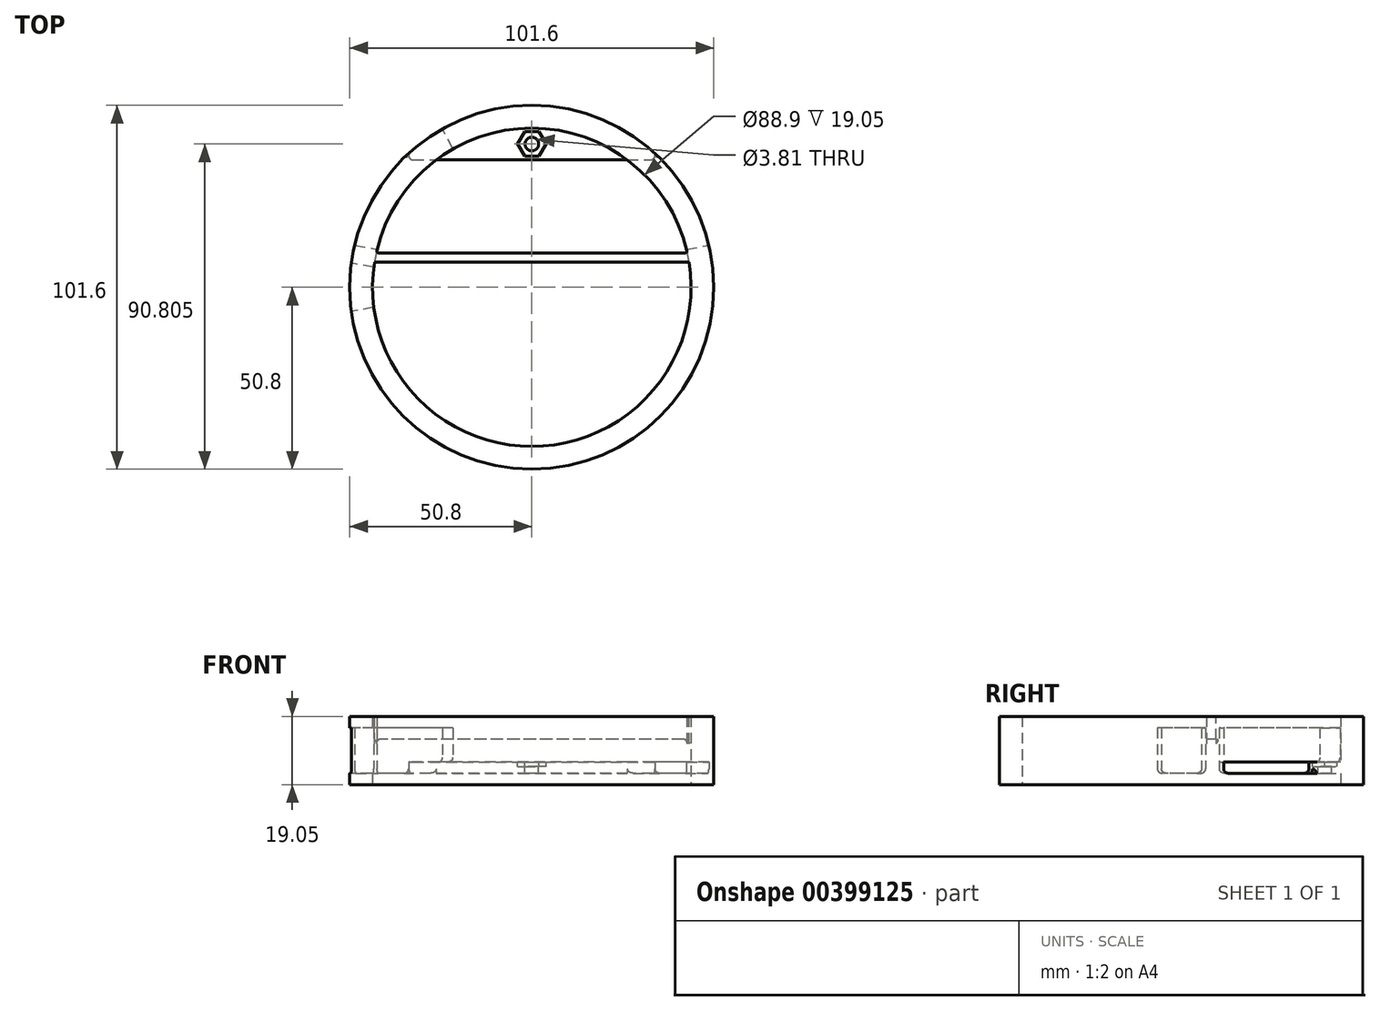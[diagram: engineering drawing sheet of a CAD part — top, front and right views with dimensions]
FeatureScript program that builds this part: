
annotation { "Feature Type Name" : "Feature", "Feature Type Description" : "" }
export const myFeature = defineFeature(function(context is Context, id is Id, definition is map)
    precondition{}
    {
        {
            var Q0;
            Q0=qCreatedBy(makeId("Top.planeOp"),FACE);
            var sketch = newSketch(context, id + "F0", { "sketchPlane" : qUnion([Q0])});
            skCircle(sketch, "E0", {"center": v(0, 0) * mm, "radius": 50.8 * mm});
            skCircle(sketch, "E1", {"center": v(0, 0) * mm, "radius": 44.45 * mm});
            skSolve(sketch);
        }
        {
            var Q0;
            Q0 = qSketchRegion(id + "F0", true);
            extrude(context, id + "F1", {"entities" : qUnion([Q0]), "depth" : 6.35 * mm});
        }
        {
            var Q0;
            Q0=makeQuery(id+"F1.opExtrude","CAP_FACE",FACE,{"disambiguationData":[OSD([sQuery(id+"F0.wireOp",EDGE,"E0"),sQuery(id+"F0.wireOp",EDGE,"E1")])],"isStart":false});
            var sketch = newSketch(context, id + "F2", { "sketchPlane" : qUnion([Q0])});
            skArc(sketch, "E2.0", {"start": v(26.67, 35.56) * mm, "mid": v(0, 44.45) * mm, "end": v(-26.67, 35.56) * mm});
            skLineSegment(sketch, "E3", {"start": v(-26.67, 35.56) * mm, "end": v(26.67, 35.56) * mm});
            skSolve(sketch);
        }
        {
            var Q0;
            Q0 = qSketchRegion(id + "F2", true);
            extrude(context, id + "F3", {"entities" : qUnion([Q0]), "operationType" : NewBodyOperationType.ADD, "oppositeDirection" : true, "depth" : 3.17 * mm});
        }
        {
            var Q0;
            {var subQ0=sQuery(id+"F2.wireOp",EDGE,"E3");var subQ1=sQuery(id+"F2.wireOp",EDGE,"E2.0");Q0=makeQuery(id+"FSnzgjkxEc41RKG_1.1.F3.boolean.opBoolean","MERGE",FACE,{"derivedFrom":[makeQuery(id+"F3.boolean.opBoolean","MERGE",FACE,{"derivedFrom":[makeQuery(id+"F1.opExtrude","CAP_FACE",FACE,{"disambiguationData":[OSD([sQuery(id+"F0.wireOp",EDGE,"E0"),sQuery(id+"F0.wireOp",EDGE,"E1")])],"isStart":false}),makeQuery(id+"F3.opExtrude","CAP_FACE",FACE,{"disambiguationData":[OSD([subQ1,subQ0])],"isStart":true})]}),makeQuery(id+"FSnzgjkxEc41RKG_1.1.F3.opExtrude","CAP_FACE",FACE,{"disambiguationData":[OSD([subQ1,subQ0])],"isStart":true})]});}
            var sketch = newSketch(context, id + "F4", { "sketchPlane" : qUnion([Q0])});
            skCircle(sketch, "E4.cCircle", {"center": v(0, 40) * mm, "radius": 3.43 * mm, "construction": true});
            skLineSegment(sketch, "E4.0", {"start": v(-1.98, 43.43) * mm, "end": v(1.98, 43.43) * mm});
            skLineSegment(sketch, "E4.1", {"start": v(1.98, 43.43) * mm, "end": v(3.96, 40) * mm});
            skLineSegment(sketch, "E4.2", {"start": v(3.96, 40) * mm, "end": v(1.98, 36.58) * mm});
            skLineSegment(sketch, "E4.3", {"start": v(1.98, 36.58) * mm, "end": v(-1.98, 36.58) * mm});
            skLineSegment(sketch, "E4.4", {"start": v(-1.98, 36.58) * mm, "end": v(-3.96, 40) * mm});
            skLineSegment(sketch, "E4.5", {"start": v(-3.96, 40) * mm, "end": v(-1.98, 43.43) * mm});
            skPoint(sketch, "E4.0.midPoint", {"position": v(0, 43.43) * mm});
            skSolve(sketch);
        }
        {
            var Q0;
            Q0 = qSketchRegion(id + "F4", true);
            extrude(context, id + "F5", {"entities" : qUnion([Q0]), "operationType" : NewBodyOperationType.REMOVE, "oppositeDirection" : true, "depth" : 1.27 * mm});
        }
        {
            var Q0;
            {var subQ0=sQuery(id+"F2.wireOp",EDGE,"E3");var subQ1=sQuery(id+"F2.wireOp",EDGE,"E2.0");Q0=makeQuery(id+"FSnzgjkxEc41RKG_1.1.F3.boolean.opBoolean","MERGE",FACE,{"derivedFrom":[makeQuery(id+"F3.boolean.opBoolean","MERGE",FACE,{"derivedFrom":[makeQuery(id+"F1.opExtrude","CAP_FACE",FACE,{"disambiguationData":[OSD([sQuery(id+"F0.wireOp",EDGE,"E0"),sQuery(id+"F0.wireOp",EDGE,"E1")])],"isStart":false}),makeQuery(id+"F3.opExtrude","CAP_FACE",FACE,{"disambiguationData":[OSD([subQ1,subQ0])],"isStart":true})]}),makeQuery(id+"FSnzgjkxEc41RKG_1.1.F3.opExtrude","CAP_FACE",FACE,{"disambiguationData":[OSD([subQ1,subQ0])],"isStart":true})]});}
            var sketch = newSketch(context, id + "F6", { "sketchPlane" : qUnion([Q0])});
            skCircle(sketch, "E5", {"center": v(0, 40) * mm, "radius": 3.43 * mm, "construction": true});
            skCircle(sketch, "E6", {"center": v(0, 40) * mm, "radius": 1.9 * mm});
            skSolve(sketch);
        }
        {
            var Q0;
            Q0 = qSketchRegion(id + "F6", true);
            extrude(context, id + "F7", {"entities" : qUnion([Q0]), "operationType" : NewBodyOperationType.REMOVE, "endBound" : BoundingType.THROUGH_ALL, "oppositeDirection" : true, "depth" : 25.4 * mm});
        }
        {
            var Q0;
            {var subQ0=sQuery(id+"F2.wireOp",EDGE,"E3");var subQ1=sQuery(id+"F2.wireOp",EDGE,"E2.0");Q0=makeQuery(id+"FSnzgjkxEc41RKG_1.1.F3.boolean.opBoolean","MERGE",FACE,{"derivedFrom":[makeQuery(id+"F3.boolean.opBoolean","MERGE",FACE,{"derivedFrom":[makeQuery(id+"F1.opExtrude","CAP_FACE",FACE,{"disambiguationData":[OSD([sQuery(id+"F0.wireOp",EDGE,"E0"),sQuery(id+"F0.wireOp",EDGE,"E1")])],"isStart":false}),makeQuery(id+"F3.opExtrude","CAP_FACE",FACE,{"disambiguationData":[OSD([subQ1,subQ0])],"isStart":true})]}),makeQuery(id+"FSnzgjkxEc41RKG_1.1.F3.opExtrude","CAP_FACE",FACE,{"disambiguationData":[OSD([subQ1,subQ0])],"isStart":true})]});}
            var sketch = newSketch(context, id + "F8", { "sketchPlane" : qUnion([Q0])});
            skCircle(sketch, "E7", {"center": v(0, 0) * mm, "radius": 44.45 * mm});
            skCircle(sketch, "E8.0", {"center": v(0, 0) * mm, "radius": 50.8 * mm});
            skSolve(sketch);
        }
        {
            var Q0;
            Q0 = qSketchRegion(id + "F8", true);
            extrude(context, id + "F9", {"entities" : qUnion([Q0]), "operationType" : NewBodyOperationType.ADD, "depth" : 9.52 * mm});
        }
        {
            var Q0;
            Q0=makeQuery(id+"F9.opExtrude","CAP_FACE",FACE,{"disambiguationData":[OSD([sQuery(id+"F8.wireOp",EDGE,"E7"),sQuery(id+"F8.wireOp",EDGE,"E8.0")])],"isStart":false});
            var sketch = newSketch(context, id + "F10", { "sketchPlane" : qUnion([Q0])});
            skLineSegment(sketch, "E9", {"start": v(0, 0) * mm, "end": v(-63.41, 11.75) * mm, "construction": true});
            skLineSegment(sketch, "E10", {"start": v(0, 0) * mm, "end": v(-59.62, -11.05) * mm, "construction": true});
            skLineSegment(sketch, "E11.0", {"start": v(-13.94, 0) * mm, "end": v(-56.67, 7.92) * mm});
            skLineSegment(sketch, "E11.1", {"start": v(-13.94, 0) * mm, "end": v(-56.67, -7.92) * mm});
            skLineSegment(sketch, "E12", {"start": v(-56.67, 7.92) * mm, "end": v(-56.67, -7.92) * mm});
            skSolve(sketch);
        }
        {
            var Q0;
            Q0 = qSketchRegion(id + "F10", true);
            extrude(context, id + "F11", {"entities" : qUnion([Q0]), "operationType" : NewBodyOperationType.REMOVE, "oppositeDirection" : true, "depth" : 12.7 * mm});
        }
        {
            var Q0;
            {var subQ0=sQuery(id+"F8.wireOp",EDGE,"E8.0");var subQ1=sQuery(id+"F8.wireOp",EDGE,"E7");var subQ2=sQuery(id+"F10.wireOp",EDGE,"E11.0");Q0=makeQuery(id+"FhbBnn4UNNE0YMo_1.1.F11.boolean.opBoolean","SPLIT",FACE,{"disambiguationData":[TD([makeQuery(id+"F11.boolean.opBoolean","COPY",FACE,{"derivedFrom":makeQuery(id+"F11.opExtrude","SWEPT_FACE",FACE,{"disambiguationData":[OSD([subQ2])]})})])],"derivedFrom":makeQuery(id+"F9.opExtrude","CAP_FACE",FACE,{"disambiguationData":[OSD([subQ1,subQ0])],"isStart":false})});}
            var sketch = newSketch(context, id + "F12", { "sketchPlane" : qUnion([Q0])});
            skLineSegment(sketch, "E13", {"start": v(0, 0) * mm, "end": v(-71.1, 13.18) * mm, "construction": true});
            skLineSegment(sketch, "E14", {"start": v(0, 0) * mm, "end": v(-37.63, 75.47) * mm, "construction": true});
            skLineSegment(sketch, "E15", {"start": v(0, 0) * mm, "end": v(32.82, 65.83) * mm, "construction": true});
            skLineSegment(sketch, "E16", {"start": v(0, 0) * mm, "end": v(69.72, 12.92) * mm, "construction": true});
            skLineSegment(sketch, "E17.0", {"start": v(-4.55, 3.43) * mm, "end": v(-70.64, 15.68) * mm});
            skLineSegment(sketch, "E17.1", {"start": v(-4.55, 3.43) * mm, "end": v(-39.9, 74.34) * mm});
            skLineSegment(sketch, "E18", {"start": v(-70.64, 15.68) * mm, "end": v(-39.9, 74.34) * mm});
            skSolve(sketch);
        }
        {
            var Q0;
            Q0 = qSketchRegion(id + "F12", true);
            extrude(context, id + "F13", {"entities" : qUnion([Q0]), "operationType" : NewBodyOperationType.REMOVE, "oppositeDirection" : true, "depth" : 9.52 * mm});
        }
        {
            var Q0;
            {var subQ0=sQuery(id+"F8.wireOp",EDGE,"E8.0");var subQ3=sQuery(id+"F8.wireOp",EDGE,"E7");var subQ6=sQuery(id+"F10.wireOp",EDGE,"a1e89873-3dcd-4c17-85da-7e8fd822ef45.trimOffspring");var subQ7=sQuery(id+"F10.wireOp",EDGE,"d77f24c4-0a5e-4d3f-a347-8b9b99c9554e.trimOffspring");var subQ8=makeQuery(id+"Fx6gkQfNs0H8Hmn_1.6.F11.opExtrude","SWEPT_FACE",FACE,{"disambiguationData":[OSD([subQ7])]});var subQ9=makeQuery(id+"F11.boolean.opBoolean","COPY",FACE,{"derivedFrom":makeQuery(id+"F11.opExtrude","SWEPT_FACE",FACE,{"disambiguationData":[OSD([subQ6])]})});Q0=makeQuery(id+"Fx6gkQfNs0H8Hmn_1.7.F11.boolean.opBoolean","SPLIT",FACE,{"disambiguationData":[TD([makeQuery(id+"Fx6gkQfNs0H8Hmn_1.6.F11.boolean.opBoolean","COPY",FACE,{"derivedFrom":subQ8})])],"derivedFrom":makeQuery(id+"Fx6gkQfNs0H8Hmn_1.6.F11.boolean.opBoolean","SPLIT",FACE,{"disambiguationData":[TD([subQ9])],"derivedFrom":makeQuery(id+"Fx6gkQfNs0H8Hmn_1.5.F11.boolean.opBoolean","SPLIT",FACE,{"disambiguationData":[TD([subQ9])],"derivedFrom":makeQuery(id+"Fx6gkQfNs0H8Hmn_1.4.F11.boolean.opBoolean","SPLIT",FACE,{"disambiguationData":[TD([subQ9])],"derivedFrom":makeQuery(id+"Fx6gkQfNs0H8Hmn_1.3.F11.boolean.opBoolean","SPLIT",FACE,{"disambiguationData":[TD([subQ9])],"derivedFrom":makeQuery(id+"Fx6gkQfNs0H8Hmn_1.2.F11.boolean.opBoolean","SPLIT",FACE,{"disambiguationData":[TD([subQ9])],"derivedFrom":makeQuery(id+"Fx6gkQfNs0H8Hmn_1.1.F11.boolean.opBoolean","SPLIT",FACE,{"disambiguationData":[TD([subQ9])],"derivedFrom":makeQuery(id+"F9.opExtrude","CAP_FACE",FACE,{"disambiguationData":[OSD([subQ3,subQ0])],"isStart":false})})})})})})})});}
            var sketch = newSketch(context, id + "F14", { "sketchPlane" : qUnion([Q0])});
            skCircle(sketch, "E19", {"center": v(0, 0) * mm, "radius": 44.45 * mm});
            skCircle(sketch, "E20", {"center": v(0, 0) * mm, "radius": 50.8 * mm});
            skSolve(sketch);
        }
        {
            var Q0;
            Q0 = qSketchRegion(id + "F14", true);
            extrude(context, id + "F15", {"entities" : qUnion([Q0]), "operationType" : NewBodyOperationType.ADD, "depth" : 3.17 * mm});
        }
        {
            var Q0;
            Q0=makeQuery(id+"F15.opExtrude","CAP_FACE",FACE,{"disambiguationData":[OSD([sQuery(id+"F14.wireOp",EDGE,"E19"),sQuery(id+"F14.wireOp",EDGE,"E20")])],"isStart":false});
            var sketch = newSketch(context, id + "F16", { "sketchPlane" : qUnion([Q0])});
            skLineSegment(sketch, "E21.bottom", {"start": v(43.89, 7.06) * mm, "end": v(-43.89, 7.06) * mm});
            skLineSegment(sketch, "E21.top", {"start": v(43.89, 9.6) * mm, "end": v(-43.89, 9.6) * mm});
            skLineSegment(sketch, "E21.left", {"start": v(43.89, 7.06) * mm, "end": v(43.89, 9.6) * mm});
            skLineSegment(sketch, "E21.right", {"start": v(-43.89, 7.06) * mm, "end": v(-43.89, 9.6) * mm});
            skPoint(sketch, "E21.middle", {"position": v(0, 8.33) * mm});
            skSolve(sketch);
        }
        {
            var Q0;
            Q0 = qSketchRegion(id + "F16", true);
            extrude(context, id + "F17", {"entities" : qUnion([Q0]), "operationType" : NewBodyOperationType.ADD, "oppositeDirection" : true, "depth" : 6.35 * mm});
        }
        {
            var Q0;
            {var subQ0=sQuery(id+"F12.wireOp",EDGE,"E18");var subQ1=sQuery(id+"F12.wireOp",EDGE,"E17.1");var subQ2=sQuery(id+"F12.wireOp",EDGE,"E17.0");var subQ3=sQuery(id+"F2.wireOp",EDGE,"E3");var subQ4=sQuery(id+"F0.wireOp",EDGE,"E1");var subQ5=sQuery(id+"F2.wireOp",EDGE,"E2.0");Q0=makeQuery(id+"FV3vAcjhJecL5uw_1.2.F13.boolean.opBoolean","MERGE",FACE,{"derivedFrom":[makeQuery(id+"FV3vAcjhJecL5uw_1.1.F13.boolean.opBoolean","MERGE",FACE,{"derivedFrom":[makeQuery(id+"F13.boolean.opBoolean","MERGE",FACE,{"derivedFrom":[makeQuery(id+"F9.boolean.opBoolean","SPLIT",FACE,{"disambiguationData":[TD([makeQuery(id+"F3.opExtrude","SWEPT_FACE",FACE,{"disambiguationData":[OSD([subQ3])]})])],"derivedFrom":makeQuery(id+"FSnzgjkxEc41RKG_1.1.F3.boolean.opBoolean","MERGE",FACE,{"derivedFrom":[makeQuery(id+"F3.boolean.opBoolean","MERGE",FACE,{"derivedFrom":[makeQuery(id+"F1.opExtrude","CAP_FACE",FACE,{"disambiguationData":[OSD([sQuery(id+"F0.wireOp",EDGE,"E0"),subQ4])],"isStart":false}),makeQuery(id+"F3.opExtrude","CAP_FACE",FACE,{"disambiguationData":[OSD([subQ5,subQ3])],"isStart":true})]}),makeQuery(id+"FSnzgjkxEc41RKG_1.1.F3.opExtrude","CAP_FACE",FACE,{"disambiguationData":[OSD([subQ5,subQ3])],"isStart":true})]})}),makeQuery(id+"F13.opExtrude","CAP_FACE",FACE,{"disambiguationData":[OSD([subQ2,subQ1,subQ0])],"isStart":false})]}),makeQuery(id+"FV3vAcjhJecL5uw_1.1.F13.opExtrude","CAP_FACE",FACE,{"disambiguationData":[OSD([subQ2,subQ1,subQ0])],"isStart":false})]}),makeQuery(id+"FV3vAcjhJecL5uw_1.2.F13.opExtrude","CAP_FACE",FACE,{"disambiguationData":[OSD([subQ2,subQ1,subQ0])],"isStart":false})]});}
            var sketch = newSketch(context, id + "F18", { "sketchPlane" : qUnion([Q0])});
            skLineSegment(sketch, "E22", {"start": v(26.67, 35.56) * mm, "end": v(61.85, 35.56) * mm});
            skLineSegment(sketch, "E23", {"start": v(26.67, 7.53) * mm, "end": v(26.67, 35.56) * mm});
            skLineSegment(sketch, "E24", {"start": v(61.85, 14.05) * mm, "end": v(61.85, 35.56) * mm});
            skLineSegment(sketch, "E25", {"start": v(26.67, 7.53) * mm, "end": v(61.85, 14.05) * mm});
            skLineSegment(sketch, "E26", {"start": v(-26.67, 35.56) * mm, "end": v(-61.52, 35.56) * mm});
            skLineSegment(sketch, "E27", {"start": v(-61.52, 35.56) * mm, "end": v(-61.52, 13.99) * mm});
            skLineSegment(sketch, "E28", {"start": v(-26.67, 35.56) * mm, "end": v(-26.67, 7.53) * mm});
            skLineSegment(sketch, "E29", {"start": v(-61.52, 13.99) * mm, "end": v(-26.67, 7.53) * mm});
            skSolve(sketch);
        }
        {
            var Q0;
            Q0 = qSketchRegion(id + "F18", true);
            extrude(context, id + "F19", {"entities" : qUnion([Q0]), "operationType" : NewBodyOperationType.REMOVE, "oppositeDirection" : true, "depth" : 3.17 * mm});
        }
        {
            var Q0;
            Q0=makeQuery(id+"F19.boolean.opBoolean","INTERSECT",EDGE,{"derivedFrom":[makeQuery(id+"F15.boolean.opBoolean","MERGE",FACE,{"derivedFrom":[makeQuery(id+"F9.boolean.opBoolean","MERGE",FACE,{"derivedFrom":[makeQuery(id+"F1.opExtrude","SWEPT_FACE",FACE,{"disambiguationData":[OSD([sQuery(id+"F0.wireOp",EDGE,"E0")])]}),makeQuery(id+"F9.opExtrude","SWEPT_FACE",FACE,{"disambiguationData":[OSD([sQuery(id+"F8.wireOp",EDGE,"E8.0")])]})]}),makeQuery(id+"F15.opExtrude","SWEPT_FACE",FACE,{"disambiguationData":[OSD([sQuery(id+"F14.wireOp",EDGE,"E20")])]})]}),makeQuery(id+"F19.opExtrude","SWEPT_FACE",FACE,{"disambiguationData":[OSD([sQuery(id+"F18.wireOp",EDGE,"E22")])]})]});
            var Q1;
            Q1=makeQuery(id+"F2eUEIhUgED1yj1_1.1.F19.boolean.opBoolean","INTERSECT",EDGE,{"derivedFrom":[makeQuery(id+"F15.boolean.opBoolean","MERGE",FACE,{"derivedFrom":[makeQuery(id+"F9.boolean.opBoolean","MERGE",FACE,{"derivedFrom":[makeQuery(id+"F1.opExtrude","SWEPT_FACE",FACE,{"disambiguationData":[OSD([sQuery(id+"F0.wireOp",EDGE,"E0")])]}),makeQuery(id+"F9.opExtrude","SWEPT_FACE",FACE,{"disambiguationData":[OSD([sQuery(id+"F8.wireOp",EDGE,"E8.0")])]})]}),makeQuery(id+"F15.opExtrude","SWEPT_FACE",FACE,{"disambiguationData":[OSD([sQuery(id+"F14.wireOp",EDGE,"E20")])]})]}),makeQuery(id+"F2eUEIhUgED1yj1_1.1.F19.opExtrude","SWEPT_FACE",FACE,{"disambiguationData":[OSD([sQuery(id+"F18.wireOp",EDGE,"E22")])]})]});
            var Q2;
            Q2=makeQuery(id+"F2eUEIhUgED1yj1_1.1.F19.boolean.opBoolean","INTERSECT",EDGE,{"derivedFrom":[makeQuery(id+"F15.boolean.opBoolean","MERGE",FACE,{"derivedFrom":[makeQuery(id+"F9.boolean.opBoolean","MERGE",FACE,{"derivedFrom":[makeQuery(id+"F1.opExtrude","SWEPT_FACE",FACE,{"disambiguationData":[OSD([sQuery(id+"F0.wireOp",EDGE,"E0")])]}),makeQuery(id+"F9.opExtrude","SWEPT_FACE",FACE,{"disambiguationData":[OSD([sQuery(id+"F8.wireOp",EDGE,"E8.0")])]})]}),makeQuery(id+"F15.opExtrude","SWEPT_FACE",FACE,{"disambiguationData":[OSD([sQuery(id+"F14.wireOp",EDGE,"E20")])]})]}),makeQuery(id+"F2eUEIhUgED1yj1_1.1.F19.opExtrude","SWEPT_FACE",FACE,{"disambiguationData":[OSD([sQuery(id+"F18.wireOp",EDGE,"E26")])]})]});
            var Q3;
            Q3=makeQuery(id+"F19.boolean.opBoolean","INTERSECT",EDGE,{"derivedFrom":[makeQuery(id+"F15.boolean.opBoolean","MERGE",FACE,{"derivedFrom":[makeQuery(id+"F9.boolean.opBoolean","MERGE",FACE,{"derivedFrom":[makeQuery(id+"F1.opExtrude","SWEPT_FACE",FACE,{"disambiguationData":[OSD([sQuery(id+"F0.wireOp",EDGE,"E0")])]}),makeQuery(id+"F9.opExtrude","SWEPT_FACE",FACE,{"disambiguationData":[OSD([sQuery(id+"F8.wireOp",EDGE,"E8.0")])]})]}),makeQuery(id+"F15.opExtrude","SWEPT_FACE",FACE,{"disambiguationData":[OSD([sQuery(id+"F14.wireOp",EDGE,"E20")])]})]}),makeQuery(id+"F19.opExtrude","SWEPT_FACE",FACE,{"disambiguationData":[OSD([sQuery(id+"F18.wireOp",EDGE,"E26")])]})]});
            fillet(context, id + "F20", {"entities" : qUnion([Q0, Q1, Q2, Q3]), "radius" : 1.27 * mm, "allowEdgeOverflow" : false});
        }
        {
            var Q0;
            Q0=makeQuery(id+"FAmw6PLWARKAkms_1.1.F13.boolean.opBoolean","COPY",EDGE,{"derivedFrom":makeQuery(id+"FAmw6PLWARKAkms_1.1.F13.opExtrude","CAP_EDGE",EDGE,{"disambiguationData":[OSD([sQuery(id+"F12.wireOp",EDGE,"E17.0")])],"isStart":true})});
            var Q1;
            Q1=makeQuery(id+"FAmw6PLWARKAkms_1.1.F13.boolean.opBoolean","COPY",EDGE,{"derivedFrom":makeQuery(id+"FAmw6PLWARKAkms_1.1.F13.opExtrude","CAP_EDGE",EDGE,{"disambiguationData":[OSD([sQuery(id+"F12.wireOp",EDGE,"E17.1")])],"isStart":true})});
            var Q2;
            Q2=makeQuery(id+"FAmw6PLWARKAkms_1.1.F13.boolean.opBoolean","COPY",EDGE,{"derivedFrom":makeQuery(id+"FAmw6PLWARKAkms_1.1.F13.opExtrude","CAP_EDGE",EDGE,{"disambiguationData":[OSD([sQuery(id+"F12.wireOp",EDGE,"E17.1")])],"isStart":false})});
            var Q3;
            Q3=makeQuery(id+"FPH29GYt6Bfk9Ch_1.1.FAmw6PLWARKAkms_1.1.F13.boolean.opBoolean","COPY",EDGE,{"derivedFrom":makeQuery(id+"FPH29GYt6Bfk9Ch_1.1.FAmw6PLWARKAkms_1.1.F13.opExtrude","CAP_EDGE",EDGE,{"disambiguationData":[OSD([sQuery(id+"F12.wireOp",EDGE,"E17.1")])],"isStart":false})});
            var Q4;
            Q4=makeQuery(id+"FPH29GYt6Bfk9Ch_1.1.FAmw6PLWARKAkms_1.1.F13.boolean.opBoolean","COPY",EDGE,{"derivedFrom":makeQuery(id+"FPH29GYt6Bfk9Ch_1.1.FAmw6PLWARKAkms_1.1.F13.opExtrude","CAP_EDGE",EDGE,{"disambiguationData":[OSD([sQuery(id+"F12.wireOp",EDGE,"E17.1")])],"isStart":true})});
            var Q5;
            Q5=makeQuery(id+"FPH29GYt6Bfk9Ch_1.1.FAmw6PLWARKAkms_1.1.F13.boolean.opBoolean","COPY",EDGE,{"derivedFrom":makeQuery(id+"FPH29GYt6Bfk9Ch_1.1.FAmw6PLWARKAkms_1.1.F13.opExtrude","CAP_EDGE",EDGE,{"disambiguationData":[OSD([sQuery(id+"F12.wireOp",EDGE,"E17.0")])],"isStart":false})});
            var Q6;
            Q6=makeQuery(id+"FPH29GYt6Bfk9Ch_1.2.FAmw6PLWARKAkms_1.1.F13.boolean.opBoolean","COPY",EDGE,{"derivedFrom":makeQuery(id+"FPH29GYt6Bfk9Ch_1.2.FAmw6PLWARKAkms_1.1.F13.opExtrude","CAP_EDGE",EDGE,{"disambiguationData":[OSD([sQuery(id+"F12.wireOp",EDGE,"E17.1")])],"isStart":true})});
            var Q7;
            Q7=makeQuery(id+"FPH29GYt6Bfk9Ch_1.2.FAmw6PLWARKAkms_1.1.F13.boolean.opBoolean","COPY",EDGE,{"derivedFrom":makeQuery(id+"FPH29GYt6Bfk9Ch_1.2.FAmw6PLWARKAkms_1.1.F13.opExtrude","CAP_EDGE",EDGE,{"disambiguationData":[OSD([sQuery(id+"F12.wireOp",EDGE,"E17.0")])],"isStart":true})});
            var Q8;
            Q8=makeQuery(id+"FPH29GYt6Bfk9Ch_1.2.FAmw6PLWARKAkms_1.1.F13.boolean.opBoolean","COPY",EDGE,{"derivedFrom":makeQuery(id+"FPH29GYt6Bfk9Ch_1.2.FAmw6PLWARKAkms_1.1.F13.opExtrude","CAP_EDGE",EDGE,{"disambiguationData":[OSD([sQuery(id+"F12.wireOp",EDGE,"E17.0")])],"isStart":false})});
            var Q9;
            Q9=makeQuery(id+"FV3vAcjhJecL5uw_1.1.F13.boolean.opBoolean","COPY",EDGE,{"derivedFrom":makeQuery(id+"FV3vAcjhJecL5uw_1.1.F13.opExtrude","CAP_EDGE",EDGE,{"disambiguationData":[OSD([sQuery(id+"F12.wireOp",EDGE,"E17.0")])],"isStart":false})});
            var Q10;
            Q10=makeQuery(id+"FV3vAcjhJecL5uw_1.2.F13.boolean.opBoolean","COPY",EDGE,{"derivedFrom":makeQuery(id+"FV3vAcjhJecL5uw_1.2.F13.opExtrude","CAP_EDGE",EDGE,{"disambiguationData":[OSD([sQuery(id+"F12.wireOp",EDGE,"E17.0")])],"isStart":false})});
            var Q11;
            Q11=makeQuery(id+"F11.boolean.opBoolean","COPY",EDGE,{"derivedFrom":makeQuery(id+"F11.opExtrude","CAP_EDGE",EDGE,{"disambiguationData":[OSD([sQuery(id+"F10.wireOp",EDGE,"E11.0")])],"isStart":false})});
            var Q12;
            Q12=makeQuery(id+"FhbBnn4UNNE0YMo_1.1.F11.boolean.opBoolean","COPY",EDGE,{"derivedFrom":makeQuery(id+"FhbBnn4UNNE0YMo_1.1.F11.opExtrude","CAP_EDGE",EDGE,{"disambiguationData":[OSD([sQuery(id+"F10.wireOp",EDGE,"E11.0")])],"isStart":true})});
            var Q13;
            Q13=makeQuery(id+"FV3vAcjhJecL5uw_1.2.F13.boolean.opBoolean","COPY",EDGE,{"derivedFrom":makeQuery(id+"FV3vAcjhJecL5uw_1.2.F13.opExtrude","CAP_EDGE",EDGE,{"disambiguationData":[OSD([sQuery(id+"F12.wireOp",EDGE,"E17.0")])],"isStart":true})});
            var Q14;
            Q14=makeQuery(id+"FV3vAcjhJecL5uw_1.1.F13.boolean.opBoolean","COPY",EDGE,{"derivedFrom":makeQuery(id+"FV3vAcjhJecL5uw_1.1.F13.opExtrude","CAP_EDGE",EDGE,{"disambiguationData":[OSD([sQuery(id+"F12.wireOp",EDGE,"E17.0")])],"isStart":true})});
            var Q15;
            Q15=makeQuery(id+"FV3vAcjhJecL5uw_1.2.F13.boolean.opBoolean","COPY",EDGE,{"derivedFrom":makeQuery(id+"FV3vAcjhJecL5uw_1.2.F13.opExtrude","CAP_EDGE",EDGE,{"disambiguationData":[OSD([sQuery(id+"F12.wireOp",EDGE,"E17.1")])],"isStart":true})});
            var Q16;
            Q16=makeQuery(id+"FhbBnn4UNNE0YMo_1.1.F11.boolean.opBoolean","COPY",EDGE,{"derivedFrom":makeQuery(id+"FhbBnn4UNNE0YMo_1.1.F11.opExtrude","CAP_EDGE",EDGE,{"disambiguationData":[OSD([sQuery(id+"F10.wireOp",EDGE,"E11.1")])],"isStart":true})});
            var Q17;
            Q17=makeQuery(id+"F13.boolean.opBoolean","COPY",EDGE,{"derivedFrom":makeQuery(id+"F13.opExtrude","CAP_EDGE",EDGE,{"disambiguationData":[OSD([sQuery(id+"F12.wireOp",EDGE,"E17.0")])],"isStart":true})});
            var Q18;
            Q18=makeQuery(id+"F11.boolean.opBoolean","COPY",EDGE,{"derivedFrom":makeQuery(id+"F11.opExtrude","CAP_EDGE",EDGE,{"disambiguationData":[OSD([sQuery(id+"F10.wireOp",EDGE,"E11.1")])],"isStart":true})});
            var Q19;
            Q19=makeQuery(id+"FhbBnn4UNNE0YMo_1.1.F11.boolean.opBoolean","COPY",EDGE,{"derivedFrom":makeQuery(id+"FhbBnn4UNNE0YMo_1.1.F11.opExtrude","CAP_EDGE",EDGE,{"disambiguationData":[OSD([sQuery(id+"F10.wireOp",EDGE,"E11.1")])],"isStart":false})});
            var Q20;
            Q20=makeQuery(id+"FPH29GYt6Bfk9Ch_1.1.FAmw6PLWARKAkms_1.1.F13.boolean.opBoolean","COPY",EDGE,{"derivedFrom":makeQuery(id+"FPH29GYt6Bfk9Ch_1.1.FAmw6PLWARKAkms_1.1.F13.opExtrude","CAP_EDGE",EDGE,{"disambiguationData":[OSD([sQuery(id+"F12.wireOp",EDGE,"E17.0")])],"isStart":true})});
            var Q21;
            Q21=makeQuery(id+"FhbBnn4UNNE0YMo_1.1.F11.boolean.opBoolean","COPY",EDGE,{"derivedFrom":makeQuery(id+"FhbBnn4UNNE0YMo_1.1.F11.opExtrude","CAP_EDGE",EDGE,{"disambiguationData":[OSD([sQuery(id+"F10.wireOp",EDGE,"E11.0")])],"isStart":false})});
            var Q22;
            Q22=makeQuery(id+"F11.boolean.opBoolean","COPY",EDGE,{"derivedFrom":makeQuery(id+"F11.opExtrude","CAP_EDGE",EDGE,{"disambiguationData":[OSD([sQuery(id+"F10.wireOp",EDGE,"E11.1")])],"isStart":false})});
            var Q23;
            Q23=makeQuery(id+"FV3vAcjhJecL5uw_1.1.F13.boolean.opBoolean","COPY",EDGE,{"derivedFrom":makeQuery(id+"FV3vAcjhJecL5uw_1.1.F13.opExtrude","CAP_EDGE",EDGE,{"disambiguationData":[OSD([sQuery(id+"F12.wireOp",EDGE,"E17.1")])],"isStart":false})});
            var Q24;
            Q24=makeQuery(id+"FV3vAcjhJecL5uw_1.1.F13.boolean.opBoolean","COPY",EDGE,{"derivedFrom":makeQuery(id+"FV3vAcjhJecL5uw_1.1.F13.opExtrude","CAP_EDGE",EDGE,{"disambiguationData":[OSD([sQuery(id+"F12.wireOp",EDGE,"E17.1")])],"isStart":true})});
            var Q25;
            Q25=makeQuery(id+"F13.boolean.opBoolean","COPY",EDGE,{"derivedFrom":makeQuery(id+"F13.opExtrude","CAP_EDGE",EDGE,{"disambiguationData":[OSD([sQuery(id+"F12.wireOp",EDGE,"E17.1")])],"isStart":true})});
            var Q26;
            Q26=makeQuery(id+"F13.boolean.opBoolean","COPY",EDGE,{"derivedFrom":makeQuery(id+"F13.opExtrude","CAP_EDGE",EDGE,{"disambiguationData":[OSD([sQuery(id+"F12.wireOp",EDGE,"E17.1")])],"isStart":false})});
            var Q27;
            Q27=makeQuery(id+"F11.boolean.opBoolean","COPY",EDGE,{"derivedFrom":makeQuery(id+"F11.opExtrude","CAP_EDGE",EDGE,{"disambiguationData":[OSD([sQuery(id+"F10.wireOp",EDGE,"E11.0")])],"isStart":true})});
            var Q28;
            Q28=makeQuery(id+"F19.boolean.opBoolean","COPY",EDGE,{"derivedFrom":makeQuery(id+"F19.opExtrude","CAP_EDGE",EDGE,{"disambiguationData":[OSD([sQuery(id+"F18.wireOp",EDGE,"E25")])],"isStart":false})});
            var Q29;
            Q29=makeQuery(id+"F19.boolean.opBoolean","COPY",EDGE,{"derivedFrom":makeQuery(id+"F19.opExtrude","CAP_EDGE",EDGE,{"disambiguationData":[OSD([sQuery(id+"F18.wireOp",EDGE,"E29")])],"isStart":false})});
            var Q30;
            Q30=makeQuery(id+"F2eUEIhUgED1yj1_1.1.F19.boolean.opBoolean","COPY",EDGE,{"derivedFrom":makeQuery(id+"F2eUEIhUgED1yj1_1.1.F19.opExtrude","CAP_EDGE",EDGE,{"disambiguationData":[OSD([sQuery(id+"F18.wireOp",EDGE,"E29")])],"isStart":false})});
            var Q31;
            Q31=makeQuery(id+"F2eUEIhUgED1yj1_1.1.F19.boolean.opBoolean","COPY",EDGE,{"derivedFrom":makeQuery(id+"F2eUEIhUgED1yj1_1.1.F19.opExtrude","CAP_EDGE",EDGE,{"disambiguationData":[OSD([sQuery(id+"F18.wireOp",EDGE,"E25")])],"isStart":false})});
            var Q32;
            {var subQ0=sQuery(id+"F2.wireOp",EDGE,"E3");var subQ1=makeQuery(id+"F3.opExtrude","SWEPT_FACE",FACE,{"disambiguationData":[OSD([subQ0])]});var subQ11=sQuery(id+"F8.wireOp",EDGE,"E7");Q32=makeQuery(id+"FV3vAcjhJecL5uw_1.1.F13.boolean.opBoolean","SPLIT",EDGE,{"disambiguationData":[TD([subQ1])],"derivedFrom":makeQuery(id+"F9.boolean.opBoolean","SPLIT",EDGE,{"disambiguationData":[TD([subQ1])],"derivedFrom":makeQuery(id+"F9.opExtrude","CAP_EDGE",EDGE,{"disambiguationData":[OSD([subQ11])],"isStart":true})})});}
            var Q33;
            {var subQ0=sQuery(id+"F2.wireOp",EDGE,"E3");var subQ7=sQuery(id+"F12.wireOp",EDGE,"E17.1");var subQ10=sQuery(id+"F8.wireOp",EDGE,"E7");Q33=makeQuery(id+"FV3vAcjhJecL5uw_1.1.F13.boolean.opBoolean","SPLIT",EDGE,{"disambiguationData":[TD([makeQuery(id+"F13.boolean.opBoolean","COPY",FACE,{"derivedFrom":makeQuery(id+"F13.opExtrude","SWEPT_FACE",FACE,{"disambiguationData":[OSD([subQ7])]})})])],"derivedFrom":makeQuery(id+"F9.boolean.opBoolean","SPLIT",EDGE,{"disambiguationData":[TD([makeQuery(id+"F3.opExtrude","SWEPT_FACE",FACE,{"disambiguationData":[OSD([subQ0])]})])],"derivedFrom":makeQuery(id+"F9.opExtrude","CAP_EDGE",EDGE,{"disambiguationData":[OSD([subQ10])],"isStart":true})})});}
            var Q34;
            {var subQ0=sQuery(id+"F2.wireOp",EDGE,"E3");var subQ8=sQuery(id+"F8.wireOp",EDGE,"E7");var subQ11=sQuery(id+"F12.wireOp",EDGE,"E17.1");Q34=makeQuery(id+"FPH29GYt6Bfk9Ch_1.1.FAmw6PLWARKAkms_1.1.F13.boolean.opBoolean","SPLIT",EDGE,{"disambiguationData":[TD([makeQuery(id+"FAmw6PLWARKAkms_1.1.F13.boolean.opBoolean","COPY",FACE,{"derivedFrom":makeQuery(id+"FAmw6PLWARKAkms_1.1.F13.opExtrude","SWEPT_FACE",FACE,{"disambiguationData":[OSD([subQ11])]})})])],"derivedFrom":makeQuery(id+"F9.boolean.opBoolean","SPLIT",EDGE,{"disambiguationData":[TD([makeQuery(id+"FSnzgjkxEc41RKG_1.1.F3.opExtrude","SWEPT_FACE",FACE,{"disambiguationData":[OSD([subQ0])]})])],"derivedFrom":makeQuery(id+"F9.opExtrude","CAP_EDGE",EDGE,{"disambiguationData":[OSD([subQ8])],"isStart":true})})});}
            var Q35;
            {var subQ0=sQuery(id+"F2.wireOp",EDGE,"E3");var subQ7=makeQuery(id+"FSnzgjkxEc41RKG_1.1.F3.opExtrude","SWEPT_FACE",FACE,{"disambiguationData":[OSD([subQ0])]});var subQ8=sQuery(id+"F8.wireOp",EDGE,"E7");Q35=makeQuery(id+"FPH29GYt6Bfk9Ch_1.1.FAmw6PLWARKAkms_1.1.F13.boolean.opBoolean","SPLIT",EDGE,{"disambiguationData":[TD([subQ7])],"derivedFrom":makeQuery(id+"F9.boolean.opBoolean","SPLIT",EDGE,{"disambiguationData":[TD([subQ7])],"derivedFrom":makeQuery(id+"F9.opExtrude","CAP_EDGE",EDGE,{"disambiguationData":[OSD([subQ8])],"isStart":true})})});}
            var Q36;
            {var subQ3=sQuery(id+"F12.wireOp",EDGE,"E17.1");var subQ5=sQuery(id+"F2.wireOp",EDGE,"E3");var subQ6=makeQuery(id+"F3.opExtrude","SWEPT_FACE",FACE,{"disambiguationData":[OSD([subQ5])]});var subQ10=sQuery(id+"F0.wireOp",EDGE,"E1");var subQ30=sQuery(id+"F8.wireOp",EDGE,"E7");var subQ36=makeQuery(id+"FPH29GYt6Bfk9Ch_1.1.FAmw6PLWARKAkms_1.1.F13.opExtrude","SWEPT_FACE",FACE,{"disambiguationData":[OSD([subQ3])]});var subQ37=makeQuery(id+"FV3vAcjhJecL5uw_1.1.F13.opExtrude","SWEPT_FACE",FACE,{"disambiguationData":[OSD([subQ3])]});var subQ38=makeQuery(id+"F9.boolean.opBoolean","MERGE",FACE,{"derivedFrom":[makeQuery(id+"F1.opExtrude","SWEPT_FACE",FACE,{"disambiguationData":[OSD([subQ10])]}),makeQuery(id+"F9.opExtrude","SWEPT_FACE",FACE,{"disambiguationData":[OSD([subQ30])]})]});var subQ39=makeQuery(id+"FV3vAcjhJecL5uw_1.1.F13.boolean.opBoolean","SPLIT",FACE,{"disambiguationData":[TD([subQ6])],"derivedFrom":subQ38});var subQ40=makeQuery(id+"FV3vAcjhJecL5uw_1.2.F13.boolean.opBoolean","SPLIT",FACE,{"disambiguationData":[TD([subQ6])],"derivedFrom":subQ39});var subQ41=makeQuery(id+"FPH29GYt6Bfk9Ch_1.1.FAmw6PLWARKAkms_1.1.F13.boolean.opBoolean","SPLIT",FACE,{"disambiguationData":[TD([subQ6])],"derivedFrom":subQ40});Q36=makeQuery(id+"FmmOau0cekQBzZS_1.1.F17.boolean.opBoolean","INTERSECT",EDGE,{"disambiguationData":[OD(0.0)],"derivedFrom":[makeQuery(id+"F15.boolean.opBoolean","MERGE",FACE,{"derivedFrom":[makeQuery(id+"FV3vAcjhJecL5uw_1.1.F13.boolean.opBoolean","SPLIT",FACE,{"disambiguationData":[TD([makeQuery(id+"F13.boolean.opBoolean","COPY",FACE,{"derivedFrom":makeQuery(id+"F13.opExtrude","SWEPT_FACE",FACE,{"disambiguationData":[OSD([subQ3])]})})])],"derivedFrom":subQ38}),makeQuery(id+"FV3vAcjhJecL5uw_1.2.F13.boolean.opBoolean","SPLIT",FACE,{"disambiguationData":[TD([makeQuery(id+"FV3vAcjhJecL5uw_1.1.F13.boolean.opBoolean","COPY",FACE,{"derivedFrom":subQ37})])],"derivedFrom":subQ39}),makeQuery(id+"FPH29GYt6Bfk9Ch_1.1.FAmw6PLWARKAkms_1.1.F13.boolean.opBoolean","SPLIT",FACE,{"disambiguationData":[TD([makeQuery(id+"FAmw6PLWARKAkms_1.1.F13.boolean.opBoolean","COPY",FACE,{"derivedFrom":makeQuery(id+"FAmw6PLWARKAkms_1.1.F13.opExtrude","SWEPT_FACE",FACE,{"disambiguationData":[OSD([subQ3])]})})])],"derivedFrom":subQ40}),makeQuery(id+"FPH29GYt6Bfk9Ch_1.2.FAmw6PLWARKAkms_1.1.F13.boolean.opBoolean","SPLIT",FACE,{"disambiguationData":[TD([makeQuery(id+"FPH29GYt6Bfk9Ch_1.1.FAmw6PLWARKAkms_1.1.F13.boolean.opBoolean","COPY",FACE,{"derivedFrom":subQ36})])],"derivedFrom":subQ41}),makeQuery(id+"FPH29GYt6Bfk9Ch_1.2.FAmw6PLWARKAkms_1.1.F13.boolean.opBoolean","SPLIT",FACE,{"disambiguationData":[TD([subQ6])],"derivedFrom":subQ41}),makeQuery(id+"F15.opExtrude","SWEPT_FACE",FACE,{"disambiguationData":[OSD([sQuery(id+"F14.wireOp",EDGE,"E19")])]})]}),makeQuery(id+"FmmOau0cekQBzZS_1.1.F17.opExtrude","CAP_FACE",FACE,{"disambiguationData":[OSD([sQuery(id+"F16.wireOp",EDGE,"E21.bottom"),sQuery(id+"F16.wireOp",EDGE,"E21.top"),sQuery(id+"F16.wireOp",EDGE,"E21.left"),sQuery(id+"F16.wireOp",EDGE,"E21.right")])],"isStart":false})]});}
            var Q37;
            {var subQ3=sQuery(id+"F12.wireOp",EDGE,"E17.1");var subQ5=sQuery(id+"F2.wireOp",EDGE,"E3");var subQ6=makeQuery(id+"F3.opExtrude","SWEPT_FACE",FACE,{"disambiguationData":[OSD([subQ5])]});var subQ10=sQuery(id+"F0.wireOp",EDGE,"E1");var subQ30=sQuery(id+"F8.wireOp",EDGE,"E7");var subQ36=makeQuery(id+"FPH29GYt6Bfk9Ch_1.1.FAmw6PLWARKAkms_1.1.F13.opExtrude","SWEPT_FACE",FACE,{"disambiguationData":[OSD([subQ3])]});var subQ37=makeQuery(id+"FV3vAcjhJecL5uw_1.1.F13.opExtrude","SWEPT_FACE",FACE,{"disambiguationData":[OSD([subQ3])]});var subQ38=makeQuery(id+"F9.boolean.opBoolean","MERGE",FACE,{"derivedFrom":[makeQuery(id+"F1.opExtrude","SWEPT_FACE",FACE,{"disambiguationData":[OSD([subQ10])]}),makeQuery(id+"F9.opExtrude","SWEPT_FACE",FACE,{"disambiguationData":[OSD([subQ30])]})]});var subQ39=makeQuery(id+"FV3vAcjhJecL5uw_1.1.F13.boolean.opBoolean","SPLIT",FACE,{"disambiguationData":[TD([subQ6])],"derivedFrom":subQ38});var subQ40=makeQuery(id+"FV3vAcjhJecL5uw_1.2.F13.boolean.opBoolean","SPLIT",FACE,{"disambiguationData":[TD([subQ6])],"derivedFrom":subQ39});var subQ41=makeQuery(id+"FPH29GYt6Bfk9Ch_1.1.FAmw6PLWARKAkms_1.1.F13.boolean.opBoolean","SPLIT",FACE,{"disambiguationData":[TD([subQ6])],"derivedFrom":subQ40});Q37=makeQuery(id+"F17.boolean.opBoolean","INTERSECT",EDGE,{"disambiguationData":[OD(0.0)],"derivedFrom":[makeQuery(id+"F15.boolean.opBoolean","MERGE",FACE,{"derivedFrom":[makeQuery(id+"FV3vAcjhJecL5uw_1.1.F13.boolean.opBoolean","SPLIT",FACE,{"disambiguationData":[TD([makeQuery(id+"F13.boolean.opBoolean","COPY",FACE,{"derivedFrom":makeQuery(id+"F13.opExtrude","SWEPT_FACE",FACE,{"disambiguationData":[OSD([subQ3])]})})])],"derivedFrom":subQ38}),makeQuery(id+"FV3vAcjhJecL5uw_1.2.F13.boolean.opBoolean","SPLIT",FACE,{"disambiguationData":[TD([makeQuery(id+"FV3vAcjhJecL5uw_1.1.F13.boolean.opBoolean","COPY",FACE,{"derivedFrom":subQ37})])],"derivedFrom":subQ39}),makeQuery(id+"FPH29GYt6Bfk9Ch_1.1.FAmw6PLWARKAkms_1.1.F13.boolean.opBoolean","SPLIT",FACE,{"disambiguationData":[TD([makeQuery(id+"FAmw6PLWARKAkms_1.1.F13.boolean.opBoolean","COPY",FACE,{"derivedFrom":makeQuery(id+"FAmw6PLWARKAkms_1.1.F13.opExtrude","SWEPT_FACE",FACE,{"disambiguationData":[OSD([subQ3])]})})])],"derivedFrom":subQ40}),makeQuery(id+"FPH29GYt6Bfk9Ch_1.2.FAmw6PLWARKAkms_1.1.F13.boolean.opBoolean","SPLIT",FACE,{"disambiguationData":[TD([makeQuery(id+"FPH29GYt6Bfk9Ch_1.1.FAmw6PLWARKAkms_1.1.F13.boolean.opBoolean","COPY",FACE,{"derivedFrom":subQ36})])],"derivedFrom":subQ41}),makeQuery(id+"FPH29GYt6Bfk9Ch_1.2.FAmw6PLWARKAkms_1.1.F13.boolean.opBoolean","SPLIT",FACE,{"disambiguationData":[TD([subQ6])],"derivedFrom":subQ41}),makeQuery(id+"F15.opExtrude","SWEPT_FACE",FACE,{"disambiguationData":[OSD([sQuery(id+"F14.wireOp",EDGE,"E19")])]})]}),makeQuery(id+"F17.opExtrude","CAP_FACE",FACE,{"disambiguationData":[OSD([sQuery(id+"F16.wireOp",EDGE,"E21.bottom"),sQuery(id+"F16.wireOp",EDGE,"E21.top"),sQuery(id+"F16.wireOp",EDGE,"E21.left"),sQuery(id+"F16.wireOp",EDGE,"E21.right")])],"isStart":false})]});}
            var Q38;
            {var subQ3=sQuery(id+"F12.wireOp",EDGE,"E17.1");var subQ5=sQuery(id+"F2.wireOp",EDGE,"E3");var subQ6=makeQuery(id+"F3.opExtrude","SWEPT_FACE",FACE,{"disambiguationData":[OSD([subQ5])]});var subQ10=sQuery(id+"F0.wireOp",EDGE,"E1");var subQ30=sQuery(id+"F8.wireOp",EDGE,"E7");var subQ36=makeQuery(id+"FPH29GYt6Bfk9Ch_1.1.FAmw6PLWARKAkms_1.1.F13.opExtrude","SWEPT_FACE",FACE,{"disambiguationData":[OSD([subQ3])]});var subQ37=makeQuery(id+"FV3vAcjhJecL5uw_1.1.F13.opExtrude","SWEPT_FACE",FACE,{"disambiguationData":[OSD([subQ3])]});var subQ38=makeQuery(id+"F9.boolean.opBoolean","MERGE",FACE,{"derivedFrom":[makeQuery(id+"F1.opExtrude","SWEPT_FACE",FACE,{"disambiguationData":[OSD([subQ10])]}),makeQuery(id+"F9.opExtrude","SWEPT_FACE",FACE,{"disambiguationData":[OSD([subQ30])]})]});var subQ39=makeQuery(id+"FV3vAcjhJecL5uw_1.1.F13.boolean.opBoolean","SPLIT",FACE,{"disambiguationData":[TD([subQ6])],"derivedFrom":subQ38});var subQ40=makeQuery(id+"FV3vAcjhJecL5uw_1.2.F13.boolean.opBoolean","SPLIT",FACE,{"disambiguationData":[TD([subQ6])],"derivedFrom":subQ39});var subQ41=makeQuery(id+"FPH29GYt6Bfk9Ch_1.1.FAmw6PLWARKAkms_1.1.F13.boolean.opBoolean","SPLIT",FACE,{"disambiguationData":[TD([subQ6])],"derivedFrom":subQ40});Q38=makeQuery(id+"F17.boolean.opBoolean","INTERSECT",EDGE,{"disambiguationData":[OD(1.0)],"derivedFrom":[makeQuery(id+"F15.boolean.opBoolean","MERGE",FACE,{"derivedFrom":[makeQuery(id+"FV3vAcjhJecL5uw_1.1.F13.boolean.opBoolean","SPLIT",FACE,{"disambiguationData":[TD([makeQuery(id+"F13.boolean.opBoolean","COPY",FACE,{"derivedFrom":makeQuery(id+"F13.opExtrude","SWEPT_FACE",FACE,{"disambiguationData":[OSD([subQ3])]})})])],"derivedFrom":subQ38}),makeQuery(id+"FV3vAcjhJecL5uw_1.2.F13.boolean.opBoolean","SPLIT",FACE,{"disambiguationData":[TD([makeQuery(id+"FV3vAcjhJecL5uw_1.1.F13.boolean.opBoolean","COPY",FACE,{"derivedFrom":subQ37})])],"derivedFrom":subQ39}),makeQuery(id+"FPH29GYt6Bfk9Ch_1.1.FAmw6PLWARKAkms_1.1.F13.boolean.opBoolean","SPLIT",FACE,{"disambiguationData":[TD([makeQuery(id+"FAmw6PLWARKAkms_1.1.F13.boolean.opBoolean","COPY",FACE,{"derivedFrom":makeQuery(id+"FAmw6PLWARKAkms_1.1.F13.opExtrude","SWEPT_FACE",FACE,{"disambiguationData":[OSD([subQ3])]})})])],"derivedFrom":subQ40}),makeQuery(id+"FPH29GYt6Bfk9Ch_1.2.FAmw6PLWARKAkms_1.1.F13.boolean.opBoolean","SPLIT",FACE,{"disambiguationData":[TD([makeQuery(id+"FPH29GYt6Bfk9Ch_1.1.FAmw6PLWARKAkms_1.1.F13.boolean.opBoolean","COPY",FACE,{"derivedFrom":subQ36})])],"derivedFrom":subQ41}),makeQuery(id+"FPH29GYt6Bfk9Ch_1.2.FAmw6PLWARKAkms_1.1.F13.boolean.opBoolean","SPLIT",FACE,{"disambiguationData":[TD([subQ6])],"derivedFrom":subQ41}),makeQuery(id+"F15.opExtrude","SWEPT_FACE",FACE,{"disambiguationData":[OSD([sQuery(id+"F14.wireOp",EDGE,"E19")])]})]}),makeQuery(id+"F17.opExtrude","CAP_FACE",FACE,{"disambiguationData":[OSD([sQuery(id+"F16.wireOp",EDGE,"E21.bottom"),sQuery(id+"F16.wireOp",EDGE,"E21.top"),sQuery(id+"F16.wireOp",EDGE,"E21.left"),sQuery(id+"F16.wireOp",EDGE,"E21.right")])],"isStart":false})]});}
            var Q39;
            {var subQ3=sQuery(id+"F12.wireOp",EDGE,"E17.1");var subQ5=sQuery(id+"F2.wireOp",EDGE,"E3");var subQ6=makeQuery(id+"F3.opExtrude","SWEPT_FACE",FACE,{"disambiguationData":[OSD([subQ5])]});var subQ10=sQuery(id+"F0.wireOp",EDGE,"E1");var subQ30=sQuery(id+"F8.wireOp",EDGE,"E7");var subQ36=makeQuery(id+"FPH29GYt6Bfk9Ch_1.1.FAmw6PLWARKAkms_1.1.F13.opExtrude","SWEPT_FACE",FACE,{"disambiguationData":[OSD([subQ3])]});var subQ37=makeQuery(id+"FV3vAcjhJecL5uw_1.1.F13.opExtrude","SWEPT_FACE",FACE,{"disambiguationData":[OSD([subQ3])]});var subQ38=makeQuery(id+"F9.boolean.opBoolean","MERGE",FACE,{"derivedFrom":[makeQuery(id+"F1.opExtrude","SWEPT_FACE",FACE,{"disambiguationData":[OSD([subQ10])]}),makeQuery(id+"F9.opExtrude","SWEPT_FACE",FACE,{"disambiguationData":[OSD([subQ30])]})]});var subQ39=makeQuery(id+"FV3vAcjhJecL5uw_1.1.F13.boolean.opBoolean","SPLIT",FACE,{"disambiguationData":[TD([subQ6])],"derivedFrom":subQ38});var subQ40=makeQuery(id+"FV3vAcjhJecL5uw_1.2.F13.boolean.opBoolean","SPLIT",FACE,{"disambiguationData":[TD([subQ6])],"derivedFrom":subQ39});var subQ41=makeQuery(id+"FPH29GYt6Bfk9Ch_1.1.FAmw6PLWARKAkms_1.1.F13.boolean.opBoolean","SPLIT",FACE,{"disambiguationData":[TD([subQ6])],"derivedFrom":subQ40});Q39=makeQuery(id+"FmmOau0cekQBzZS_1.1.F17.boolean.opBoolean","INTERSECT",EDGE,{"disambiguationData":[OD(1.0)],"derivedFrom":[makeQuery(id+"F15.boolean.opBoolean","MERGE",FACE,{"derivedFrom":[makeQuery(id+"FV3vAcjhJecL5uw_1.1.F13.boolean.opBoolean","SPLIT",FACE,{"disambiguationData":[TD([makeQuery(id+"F13.boolean.opBoolean","COPY",FACE,{"derivedFrom":makeQuery(id+"F13.opExtrude","SWEPT_FACE",FACE,{"disambiguationData":[OSD([subQ3])]})})])],"derivedFrom":subQ38}),makeQuery(id+"FV3vAcjhJecL5uw_1.2.F13.boolean.opBoolean","SPLIT",FACE,{"disambiguationData":[TD([makeQuery(id+"FV3vAcjhJecL5uw_1.1.F13.boolean.opBoolean","COPY",FACE,{"derivedFrom":subQ37})])],"derivedFrom":subQ39}),makeQuery(id+"FPH29GYt6Bfk9Ch_1.1.FAmw6PLWARKAkms_1.1.F13.boolean.opBoolean","SPLIT",FACE,{"disambiguationData":[TD([makeQuery(id+"FAmw6PLWARKAkms_1.1.F13.boolean.opBoolean","COPY",FACE,{"derivedFrom":makeQuery(id+"FAmw6PLWARKAkms_1.1.F13.opExtrude","SWEPT_FACE",FACE,{"disambiguationData":[OSD([subQ3])]})})])],"derivedFrom":subQ40}),makeQuery(id+"FPH29GYt6Bfk9Ch_1.2.FAmw6PLWARKAkms_1.1.F13.boolean.opBoolean","SPLIT",FACE,{"disambiguationData":[TD([makeQuery(id+"FPH29GYt6Bfk9Ch_1.1.FAmw6PLWARKAkms_1.1.F13.boolean.opBoolean","COPY",FACE,{"derivedFrom":subQ36})])],"derivedFrom":subQ41}),makeQuery(id+"FPH29GYt6Bfk9Ch_1.2.FAmw6PLWARKAkms_1.1.F13.boolean.opBoolean","SPLIT",FACE,{"disambiguationData":[TD([subQ6])],"derivedFrom":subQ41}),makeQuery(id+"F15.opExtrude","SWEPT_FACE",FACE,{"disambiguationData":[OSD([sQuery(id+"F14.wireOp",EDGE,"E19")])]})]}),makeQuery(id+"FmmOau0cekQBzZS_1.1.F17.opExtrude","CAP_FACE",FACE,{"disambiguationData":[OSD([sQuery(id+"F16.wireOp",EDGE,"E21.bottom"),sQuery(id+"F16.wireOp",EDGE,"E21.top"),sQuery(id+"F16.wireOp",EDGE,"E21.left"),sQuery(id+"F16.wireOp",EDGE,"E21.right")])],"isStart":false})]});}
            var Q40;
            Q40=makeQuery(id+"F19.boolean.opBoolean","COPY",EDGE,{"derivedFrom":makeQuery(id+"F19.opExtrude","CAP_EDGE",EDGE,{"disambiguationData":[OSD([sQuery(id+"F18.wireOp",EDGE,"E26")])],"isStart":false})});
            var Q41;
            Q41=makeQuery(id+"F19.boolean.opBoolean","COPY",EDGE,{"derivedFrom":makeQuery(id+"F19.opExtrude","CAP_EDGE",EDGE,{"disambiguationData":[OSD([sQuery(id+"F18.wireOp",EDGE,"E22")])],"isStart":false})});
            var Q42;
            Q42=makeQuery(id+"F2eUEIhUgED1yj1_1.1.F19.boolean.opBoolean","COPY",EDGE,{"derivedFrom":makeQuery(id+"F2eUEIhUgED1yj1_1.1.F19.opExtrude","CAP_EDGE",EDGE,{"disambiguationData":[OSD([sQuery(id+"F18.wireOp",EDGE,"E26")])],"isStart":false})});
            var Q43;
            Q43=makeQuery(id+"F2eUEIhUgED1yj1_1.1.F19.boolean.opBoolean","COPY",EDGE,{"derivedFrom":makeQuery(id+"F2eUEIhUgED1yj1_1.1.F19.opExtrude","CAP_EDGE",EDGE,{"disambiguationData":[OSD([sQuery(id+"F18.wireOp",EDGE,"E22")])],"isStart":false})});
            fillet(context, id + "F21", {"entities" : qUnion([Q0, Q1, Q2, Q3, Q4, Q5, Q6, Q7, Q8, Q9, Q10, Q11, Q12, Q13, Q14, Q15, Q16, Q17, Q18, Q19, Q20, Q21, Q22, Q23, Q24, Q25, Q26, Q27, Q28, Q29, Q30, Q31, Q32, Q33, Q34, Q35, Q36, Q37, Q38, Q39, Q40, Q41, Q42, Q43]), "radius" : 1.27 * mm, "tangentPropagation" : true, "allowEdgeOverflow" : false});
        }
        {
            var Q0;
            {var subQ3=sQuery(id+"F12.wireOp",EDGE,"E17.1");var subQ5=sQuery(id+"F2.wireOp",EDGE,"E3");var subQ6=makeQuery(id+"F3.opExtrude","SWEPT_FACE",FACE,{"disambiguationData":[OSD([subQ5])]});var subQ10=sQuery(id+"F0.wireOp",EDGE,"E1");var subQ30=sQuery(id+"F8.wireOp",EDGE,"E7");var subQ36=makeQuery(id+"FPH29GYt6Bfk9Ch_1.1.FAmw6PLWARKAkms_1.1.F13.opExtrude","SWEPT_FACE",FACE,{"disambiguationData":[OSD([subQ3])]});var subQ37=makeQuery(id+"FV3vAcjhJecL5uw_1.1.F13.opExtrude","SWEPT_FACE",FACE,{"disambiguationData":[OSD([subQ3])]});var subQ38=makeQuery(id+"F9.boolean.opBoolean","MERGE",FACE,{"derivedFrom":[makeQuery(id+"F1.opExtrude","SWEPT_FACE",FACE,{"disambiguationData":[OSD([subQ10])]}),makeQuery(id+"F9.opExtrude","SWEPT_FACE",FACE,{"disambiguationData":[OSD([subQ30])]})]});var subQ39=makeQuery(id+"FV3vAcjhJecL5uw_1.1.F13.boolean.opBoolean","SPLIT",FACE,{"disambiguationData":[TD([subQ6])],"derivedFrom":subQ38});var subQ40=makeQuery(id+"FV3vAcjhJecL5uw_1.2.F13.boolean.opBoolean","SPLIT",FACE,{"disambiguationData":[TD([subQ6])],"derivedFrom":subQ39});var subQ41=makeQuery(id+"FPH29GYt6Bfk9Ch_1.1.FAmw6PLWARKAkms_1.1.F13.boolean.opBoolean","SPLIT",FACE,{"disambiguationData":[TD([subQ6])],"derivedFrom":subQ40});Q0=makeQuery(id+"F17.boolean.opBoolean","INTERSECT",EDGE,{"disambiguationData":[OD(1.0)],"derivedFrom":[makeQuery(id+"F15.boolean.opBoolean","MERGE",FACE,{"derivedFrom":[makeQuery(id+"FV3vAcjhJecL5uw_1.1.F13.boolean.opBoolean","SPLIT",FACE,{"disambiguationData":[TD([makeQuery(id+"F13.boolean.opBoolean","COPY",FACE,{"derivedFrom":makeQuery(id+"F13.opExtrude","SWEPT_FACE",FACE,{"disambiguationData":[OSD([subQ3])]})})])],"derivedFrom":subQ38}),makeQuery(id+"FV3vAcjhJecL5uw_1.2.F13.boolean.opBoolean","SPLIT",FACE,{"disambiguationData":[TD([makeQuery(id+"FV3vAcjhJecL5uw_1.1.F13.boolean.opBoolean","COPY",FACE,{"derivedFrom":subQ37})])],"derivedFrom":subQ39}),makeQuery(id+"FPH29GYt6Bfk9Ch_1.1.FAmw6PLWARKAkms_1.1.F13.boolean.opBoolean","SPLIT",FACE,{"disambiguationData":[TD([makeQuery(id+"FAmw6PLWARKAkms_1.1.F13.boolean.opBoolean","COPY",FACE,{"derivedFrom":makeQuery(id+"FAmw6PLWARKAkms_1.1.F13.opExtrude","SWEPT_FACE",FACE,{"disambiguationData":[OSD([subQ3])]})})])],"derivedFrom":subQ40}),makeQuery(id+"FPH29GYt6Bfk9Ch_1.2.FAmw6PLWARKAkms_1.1.F13.boolean.opBoolean","SPLIT",FACE,{"disambiguationData":[TD([makeQuery(id+"FPH29GYt6Bfk9Ch_1.1.FAmw6PLWARKAkms_1.1.F13.boolean.opBoolean","COPY",FACE,{"derivedFrom":subQ36})])],"derivedFrom":subQ41}),makeQuery(id+"FPH29GYt6Bfk9Ch_1.2.FAmw6PLWARKAkms_1.1.F13.boolean.opBoolean","SPLIT",FACE,{"disambiguationData":[TD([subQ6])],"derivedFrom":subQ41}),makeQuery(id+"F15.opExtrude","SWEPT_FACE",FACE,{"disambiguationData":[OSD([sQuery(id+"F14.wireOp",EDGE,"E19")])]})]}),makeQuery(id+"F17.opExtrude","SWEPT_FACE",FACE,{"disambiguationData":[OSD([sQuery(id+"F16.wireOp",EDGE,"E21.top")])]})]});}
            var Q1;
            Q1=makeQuery(id+"F17.opExtrude","SWEPT_EDGE",EDGE,{"disambiguationData":[OSD([sQuery(id+"F14.wireOp",EDGE,"E19"),sQuery(id+"F16.wireOp",EDGE,"E21.bottom"),sQuery(id+"F16.wireOp",EDGE,"E21.right")])]});
            var Q2;
            {var subQ3=sQuery(id+"F12.wireOp",EDGE,"E17.1");var subQ5=sQuery(id+"F2.wireOp",EDGE,"E3");var subQ6=makeQuery(id+"F3.opExtrude","SWEPT_FACE",FACE,{"disambiguationData":[OSD([subQ5])]});var subQ10=sQuery(id+"F0.wireOp",EDGE,"E1");var subQ30=sQuery(id+"F8.wireOp",EDGE,"E7");var subQ36=makeQuery(id+"FPH29GYt6Bfk9Ch_1.1.FAmw6PLWARKAkms_1.1.F13.opExtrude","SWEPT_FACE",FACE,{"disambiguationData":[OSD([subQ3])]});var subQ37=makeQuery(id+"FV3vAcjhJecL5uw_1.1.F13.opExtrude","SWEPT_FACE",FACE,{"disambiguationData":[OSD([subQ3])]});var subQ38=makeQuery(id+"F9.boolean.opBoolean","MERGE",FACE,{"derivedFrom":[makeQuery(id+"F1.opExtrude","SWEPT_FACE",FACE,{"disambiguationData":[OSD([subQ10])]}),makeQuery(id+"F9.opExtrude","SWEPT_FACE",FACE,{"disambiguationData":[OSD([subQ30])]})]});var subQ39=makeQuery(id+"FV3vAcjhJecL5uw_1.1.F13.boolean.opBoolean","SPLIT",FACE,{"disambiguationData":[TD([subQ6])],"derivedFrom":subQ38});var subQ40=makeQuery(id+"FV3vAcjhJecL5uw_1.2.F13.boolean.opBoolean","SPLIT",FACE,{"disambiguationData":[TD([subQ6])],"derivedFrom":subQ39});var subQ41=makeQuery(id+"FPH29GYt6Bfk9Ch_1.1.FAmw6PLWARKAkms_1.1.F13.boolean.opBoolean","SPLIT",FACE,{"disambiguationData":[TD([subQ6])],"derivedFrom":subQ40});Q2=makeQuery(id+"FmmOau0cekQBzZS_1.1.F17.boolean.opBoolean","INTERSECT",EDGE,{"disambiguationData":[OD(1.0)],"derivedFrom":[makeQuery(id+"F15.boolean.opBoolean","MERGE",FACE,{"derivedFrom":[makeQuery(id+"FV3vAcjhJecL5uw_1.1.F13.boolean.opBoolean","SPLIT",FACE,{"disambiguationData":[TD([makeQuery(id+"F13.boolean.opBoolean","COPY",FACE,{"derivedFrom":makeQuery(id+"F13.opExtrude","SWEPT_FACE",FACE,{"disambiguationData":[OSD([subQ3])]})})])],"derivedFrom":subQ38}),makeQuery(id+"FV3vAcjhJecL5uw_1.2.F13.boolean.opBoolean","SPLIT",FACE,{"disambiguationData":[TD([makeQuery(id+"FV3vAcjhJecL5uw_1.1.F13.boolean.opBoolean","COPY",FACE,{"derivedFrom":subQ37})])],"derivedFrom":subQ39}),makeQuery(id+"FPH29GYt6Bfk9Ch_1.1.FAmw6PLWARKAkms_1.1.F13.boolean.opBoolean","SPLIT",FACE,{"disambiguationData":[TD([makeQuery(id+"FAmw6PLWARKAkms_1.1.F13.boolean.opBoolean","COPY",FACE,{"derivedFrom":makeQuery(id+"FAmw6PLWARKAkms_1.1.F13.opExtrude","SWEPT_FACE",FACE,{"disambiguationData":[OSD([subQ3])]})})])],"derivedFrom":subQ40}),makeQuery(id+"FPH29GYt6Bfk9Ch_1.2.FAmw6PLWARKAkms_1.1.F13.boolean.opBoolean","SPLIT",FACE,{"disambiguationData":[TD([makeQuery(id+"FPH29GYt6Bfk9Ch_1.1.FAmw6PLWARKAkms_1.1.F13.boolean.opBoolean","COPY",FACE,{"derivedFrom":subQ36})])],"derivedFrom":subQ41}),makeQuery(id+"FPH29GYt6Bfk9Ch_1.2.FAmw6PLWARKAkms_1.1.F13.boolean.opBoolean","SPLIT",FACE,{"disambiguationData":[TD([subQ6])],"derivedFrom":subQ41}),makeQuery(id+"F15.opExtrude","SWEPT_FACE",FACE,{"disambiguationData":[OSD([sQuery(id+"F14.wireOp",EDGE,"E19")])]})]}),makeQuery(id+"FmmOau0cekQBzZS_1.1.F17.opExtrude","SWEPT_FACE",FACE,{"disambiguationData":[OSD([sQuery(id+"F16.wireOp",EDGE,"E21.top")])]})]});}
            var Q3;
            Q3=makeQuery(id+"FmmOau0cekQBzZS_1.1.F17.opExtrude","SWEPT_EDGE",EDGE,{"disambiguationData":[OSD([sQuery(id+"F14.wireOp",EDGE,"E19"),sQuery(id+"F16.wireOp",EDGE,"E21.bottom"),sQuery(id+"F16.wireOp",EDGE,"E21.right")])]});
            var Q4;
            {var subQ3=sQuery(id+"F12.wireOp",EDGE,"E17.1");var subQ5=sQuery(id+"F2.wireOp",EDGE,"E3");var subQ6=makeQuery(id+"F3.opExtrude","SWEPT_FACE",FACE,{"disambiguationData":[OSD([subQ5])]});var subQ10=sQuery(id+"F0.wireOp",EDGE,"E1");var subQ30=sQuery(id+"F8.wireOp",EDGE,"E7");var subQ36=makeQuery(id+"FPH29GYt6Bfk9Ch_1.1.FAmw6PLWARKAkms_1.1.F13.opExtrude","SWEPT_FACE",FACE,{"disambiguationData":[OSD([subQ3])]});var subQ37=makeQuery(id+"FV3vAcjhJecL5uw_1.1.F13.opExtrude","SWEPT_FACE",FACE,{"disambiguationData":[OSD([subQ3])]});var subQ38=makeQuery(id+"F9.boolean.opBoolean","MERGE",FACE,{"derivedFrom":[makeQuery(id+"F1.opExtrude","SWEPT_FACE",FACE,{"disambiguationData":[OSD([subQ10])]}),makeQuery(id+"F9.opExtrude","SWEPT_FACE",FACE,{"disambiguationData":[OSD([subQ30])]})]});var subQ39=makeQuery(id+"FV3vAcjhJecL5uw_1.1.F13.boolean.opBoolean","SPLIT",FACE,{"disambiguationData":[TD([subQ6])],"derivedFrom":subQ38});var subQ40=makeQuery(id+"FV3vAcjhJecL5uw_1.2.F13.boolean.opBoolean","SPLIT",FACE,{"disambiguationData":[TD([subQ6])],"derivedFrom":subQ39});var subQ41=makeQuery(id+"FPH29GYt6Bfk9Ch_1.1.FAmw6PLWARKAkms_1.1.F13.boolean.opBoolean","SPLIT",FACE,{"disambiguationData":[TD([subQ6])],"derivedFrom":subQ40});Q4=makeQuery(id+"FmmOau0cekQBzZS_1.1.F17.boolean.opBoolean","INTERSECT",EDGE,{"disambiguationData":[OD(0.0)],"derivedFrom":[makeQuery(id+"F15.boolean.opBoolean","MERGE",FACE,{"derivedFrom":[makeQuery(id+"FV3vAcjhJecL5uw_1.1.F13.boolean.opBoolean","SPLIT",FACE,{"disambiguationData":[TD([makeQuery(id+"F13.boolean.opBoolean","COPY",FACE,{"derivedFrom":makeQuery(id+"F13.opExtrude","SWEPT_FACE",FACE,{"disambiguationData":[OSD([subQ3])]})})])],"derivedFrom":subQ38}),makeQuery(id+"FV3vAcjhJecL5uw_1.2.F13.boolean.opBoolean","SPLIT",FACE,{"disambiguationData":[TD([makeQuery(id+"FV3vAcjhJecL5uw_1.1.F13.boolean.opBoolean","COPY",FACE,{"derivedFrom":subQ37})])],"derivedFrom":subQ39}),makeQuery(id+"FPH29GYt6Bfk9Ch_1.1.FAmw6PLWARKAkms_1.1.F13.boolean.opBoolean","SPLIT",FACE,{"disambiguationData":[TD([makeQuery(id+"FAmw6PLWARKAkms_1.1.F13.boolean.opBoolean","COPY",FACE,{"derivedFrom":makeQuery(id+"FAmw6PLWARKAkms_1.1.F13.opExtrude","SWEPT_FACE",FACE,{"disambiguationData":[OSD([subQ3])]})})])],"derivedFrom":subQ40}),makeQuery(id+"FPH29GYt6Bfk9Ch_1.2.FAmw6PLWARKAkms_1.1.F13.boolean.opBoolean","SPLIT",FACE,{"disambiguationData":[TD([makeQuery(id+"FPH29GYt6Bfk9Ch_1.1.FAmw6PLWARKAkms_1.1.F13.boolean.opBoolean","COPY",FACE,{"derivedFrom":subQ36})])],"derivedFrom":subQ41}),makeQuery(id+"FPH29GYt6Bfk9Ch_1.2.FAmw6PLWARKAkms_1.1.F13.boolean.opBoolean","SPLIT",FACE,{"disambiguationData":[TD([subQ6])],"derivedFrom":subQ41}),makeQuery(id+"F15.opExtrude","SWEPT_FACE",FACE,{"disambiguationData":[OSD([sQuery(id+"F14.wireOp",EDGE,"E19")])]})]}),makeQuery(id+"FmmOau0cekQBzZS_1.1.F17.opExtrude","SWEPT_FACE",FACE,{"disambiguationData":[OSD([sQuery(id+"F16.wireOp",EDGE,"E21.top")])]})]});}
            var Q5;
            {var subQ3=sQuery(id+"F12.wireOp",EDGE,"E17.1");var subQ5=sQuery(id+"F2.wireOp",EDGE,"E3");var subQ6=makeQuery(id+"F3.opExtrude","SWEPT_FACE",FACE,{"disambiguationData":[OSD([subQ5])]});var subQ10=sQuery(id+"F0.wireOp",EDGE,"E1");var subQ30=sQuery(id+"F8.wireOp",EDGE,"E7");var subQ36=makeQuery(id+"FPH29GYt6Bfk9Ch_1.1.FAmw6PLWARKAkms_1.1.F13.opExtrude","SWEPT_FACE",FACE,{"disambiguationData":[OSD([subQ3])]});var subQ37=makeQuery(id+"FV3vAcjhJecL5uw_1.1.F13.opExtrude","SWEPT_FACE",FACE,{"disambiguationData":[OSD([subQ3])]});var subQ38=makeQuery(id+"F9.boolean.opBoolean","MERGE",FACE,{"derivedFrom":[makeQuery(id+"F1.opExtrude","SWEPT_FACE",FACE,{"disambiguationData":[OSD([subQ10])]}),makeQuery(id+"F9.opExtrude","SWEPT_FACE",FACE,{"disambiguationData":[OSD([subQ30])]})]});var subQ39=makeQuery(id+"FV3vAcjhJecL5uw_1.1.F13.boolean.opBoolean","SPLIT",FACE,{"disambiguationData":[TD([subQ6])],"derivedFrom":subQ38});var subQ40=makeQuery(id+"FV3vAcjhJecL5uw_1.2.F13.boolean.opBoolean","SPLIT",FACE,{"disambiguationData":[TD([subQ6])],"derivedFrom":subQ39});var subQ41=makeQuery(id+"FPH29GYt6Bfk9Ch_1.1.FAmw6PLWARKAkms_1.1.F13.boolean.opBoolean","SPLIT",FACE,{"disambiguationData":[TD([subQ6])],"derivedFrom":subQ40});Q5=makeQuery(id+"FmmOau0cekQBzZS_1.1.F17.boolean.opBoolean","INTERSECT",EDGE,{"disambiguationData":[OD(0.0)],"derivedFrom":[makeQuery(id+"F15.boolean.opBoolean","MERGE",FACE,{"derivedFrom":[makeQuery(id+"FV3vAcjhJecL5uw_1.1.F13.boolean.opBoolean","SPLIT",FACE,{"disambiguationData":[TD([makeQuery(id+"F13.boolean.opBoolean","COPY",FACE,{"derivedFrom":makeQuery(id+"F13.opExtrude","SWEPT_FACE",FACE,{"disambiguationData":[OSD([subQ3])]})})])],"derivedFrom":subQ38}),makeQuery(id+"FV3vAcjhJecL5uw_1.2.F13.boolean.opBoolean","SPLIT",FACE,{"disambiguationData":[TD([makeQuery(id+"FV3vAcjhJecL5uw_1.1.F13.boolean.opBoolean","COPY",FACE,{"derivedFrom":subQ37})])],"derivedFrom":subQ39}),makeQuery(id+"FPH29GYt6Bfk9Ch_1.1.FAmw6PLWARKAkms_1.1.F13.boolean.opBoolean","SPLIT",FACE,{"disambiguationData":[TD([makeQuery(id+"FAmw6PLWARKAkms_1.1.F13.boolean.opBoolean","COPY",FACE,{"derivedFrom":makeQuery(id+"FAmw6PLWARKAkms_1.1.F13.opExtrude","SWEPT_FACE",FACE,{"disambiguationData":[OSD([subQ3])]})})])],"derivedFrom":subQ40}),makeQuery(id+"FPH29GYt6Bfk9Ch_1.2.FAmw6PLWARKAkms_1.1.F13.boolean.opBoolean","SPLIT",FACE,{"disambiguationData":[TD([makeQuery(id+"FPH29GYt6Bfk9Ch_1.1.FAmw6PLWARKAkms_1.1.F13.boolean.opBoolean","COPY",FACE,{"derivedFrom":subQ36})])],"derivedFrom":subQ41}),makeQuery(id+"FPH29GYt6Bfk9Ch_1.2.FAmw6PLWARKAkms_1.1.F13.boolean.opBoolean","SPLIT",FACE,{"disambiguationData":[TD([subQ6])],"derivedFrom":subQ41}),makeQuery(id+"F15.opExtrude","SWEPT_FACE",FACE,{"disambiguationData":[OSD([sQuery(id+"F14.wireOp",EDGE,"E19")])]})]}),makeQuery(id+"FmmOau0cekQBzZS_1.1.F17.opExtrude","CAP_FACE",FACE,{"disambiguationData":[OSD([sQuery(id+"F16.wireOp",EDGE,"E21.bottom"),sQuery(id+"F16.wireOp",EDGE,"E21.top"),sQuery(id+"F16.wireOp",EDGE,"E21.left"),sQuery(id+"F16.wireOp",EDGE,"E21.right")])],"isStart":false})]});}
            var Q6;
            Q6=makeQuery(id+"F17.opExtrude","SWEPT_EDGE",EDGE,{"disambiguationData":[OSD([sQuery(id+"F14.wireOp",EDGE,"E19"),sQuery(id+"F16.wireOp",EDGE,"E21.bottom"),sQuery(id+"F16.wireOp",EDGE,"E21.left")])]});
            var Q7;
            {var subQ3=sQuery(id+"F12.wireOp",EDGE,"E17.1");var subQ5=sQuery(id+"F2.wireOp",EDGE,"E3");var subQ6=makeQuery(id+"F3.opExtrude","SWEPT_FACE",FACE,{"disambiguationData":[OSD([subQ5])]});var subQ10=sQuery(id+"F0.wireOp",EDGE,"E1");var subQ30=sQuery(id+"F8.wireOp",EDGE,"E7");var subQ36=makeQuery(id+"FPH29GYt6Bfk9Ch_1.1.FAmw6PLWARKAkms_1.1.F13.opExtrude","SWEPT_FACE",FACE,{"disambiguationData":[OSD([subQ3])]});var subQ37=makeQuery(id+"FV3vAcjhJecL5uw_1.1.F13.opExtrude","SWEPT_FACE",FACE,{"disambiguationData":[OSD([subQ3])]});var subQ38=makeQuery(id+"F9.boolean.opBoolean","MERGE",FACE,{"derivedFrom":[makeQuery(id+"F1.opExtrude","SWEPT_FACE",FACE,{"disambiguationData":[OSD([subQ10])]}),makeQuery(id+"F9.opExtrude","SWEPT_FACE",FACE,{"disambiguationData":[OSD([subQ30])]})]});var subQ39=makeQuery(id+"FV3vAcjhJecL5uw_1.1.F13.boolean.opBoolean","SPLIT",FACE,{"disambiguationData":[TD([subQ6])],"derivedFrom":subQ38});var subQ40=makeQuery(id+"FV3vAcjhJecL5uw_1.2.F13.boolean.opBoolean","SPLIT",FACE,{"disambiguationData":[TD([subQ6])],"derivedFrom":subQ39});var subQ41=makeQuery(id+"FPH29GYt6Bfk9Ch_1.1.FAmw6PLWARKAkms_1.1.F13.boolean.opBoolean","SPLIT",FACE,{"disambiguationData":[TD([subQ6])],"derivedFrom":subQ40});Q7=makeQuery(id+"F17.boolean.opBoolean","INTERSECT",EDGE,{"disambiguationData":[OD(0.0)],"derivedFrom":[makeQuery(id+"F15.boolean.opBoolean","MERGE",FACE,{"derivedFrom":[makeQuery(id+"FV3vAcjhJecL5uw_1.1.F13.boolean.opBoolean","SPLIT",FACE,{"disambiguationData":[TD([makeQuery(id+"F13.boolean.opBoolean","COPY",FACE,{"derivedFrom":makeQuery(id+"F13.opExtrude","SWEPT_FACE",FACE,{"disambiguationData":[OSD([subQ3])]})})])],"derivedFrom":subQ38}),makeQuery(id+"FV3vAcjhJecL5uw_1.2.F13.boolean.opBoolean","SPLIT",FACE,{"disambiguationData":[TD([makeQuery(id+"FV3vAcjhJecL5uw_1.1.F13.boolean.opBoolean","COPY",FACE,{"derivedFrom":subQ37})])],"derivedFrom":subQ39}),makeQuery(id+"FPH29GYt6Bfk9Ch_1.1.FAmw6PLWARKAkms_1.1.F13.boolean.opBoolean","SPLIT",FACE,{"disambiguationData":[TD([makeQuery(id+"FAmw6PLWARKAkms_1.1.F13.boolean.opBoolean","COPY",FACE,{"derivedFrom":makeQuery(id+"FAmw6PLWARKAkms_1.1.F13.opExtrude","SWEPT_FACE",FACE,{"disambiguationData":[OSD([subQ3])]})})])],"derivedFrom":subQ40}),makeQuery(id+"FPH29GYt6Bfk9Ch_1.2.FAmw6PLWARKAkms_1.1.F13.boolean.opBoolean","SPLIT",FACE,{"disambiguationData":[TD([makeQuery(id+"FPH29GYt6Bfk9Ch_1.1.FAmw6PLWARKAkms_1.1.F13.boolean.opBoolean","COPY",FACE,{"derivedFrom":subQ36})])],"derivedFrom":subQ41}),makeQuery(id+"FPH29GYt6Bfk9Ch_1.2.FAmw6PLWARKAkms_1.1.F13.boolean.opBoolean","SPLIT",FACE,{"disambiguationData":[TD([subQ6])],"derivedFrom":subQ41}),makeQuery(id+"F15.opExtrude","SWEPT_FACE",FACE,{"disambiguationData":[OSD([sQuery(id+"F14.wireOp",EDGE,"E19")])]})]}),makeQuery(id+"F17.opExtrude","CAP_FACE",FACE,{"disambiguationData":[OSD([sQuery(id+"F16.wireOp",EDGE,"E21.bottom"),sQuery(id+"F16.wireOp",EDGE,"E21.top"),sQuery(id+"F16.wireOp",EDGE,"E21.left"),sQuery(id+"F16.wireOp",EDGE,"E21.right")])],"isStart":false})]});}
            var Q8;
            Q8=makeQuery(id+"FmmOau0cekQBzZS_1.1.F17.opExtrude","SWEPT_EDGE",EDGE,{"disambiguationData":[OSD([sQuery(id+"F14.wireOp",EDGE,"E19"),sQuery(id+"F16.wireOp",EDGE,"E21.bottom"),sQuery(id+"F16.wireOp",EDGE,"E21.left")])]});
            var Q9;
            {var subQ3=sQuery(id+"F12.wireOp",EDGE,"E17.1");var subQ5=sQuery(id+"F2.wireOp",EDGE,"E3");var subQ6=makeQuery(id+"F3.opExtrude","SWEPT_FACE",FACE,{"disambiguationData":[OSD([subQ5])]});var subQ10=sQuery(id+"F0.wireOp",EDGE,"E1");var subQ30=sQuery(id+"F8.wireOp",EDGE,"E7");var subQ36=makeQuery(id+"FPH29GYt6Bfk9Ch_1.1.FAmw6PLWARKAkms_1.1.F13.opExtrude","SWEPT_FACE",FACE,{"disambiguationData":[OSD([subQ3])]});var subQ37=makeQuery(id+"FV3vAcjhJecL5uw_1.1.F13.opExtrude","SWEPT_FACE",FACE,{"disambiguationData":[OSD([subQ3])]});var subQ38=makeQuery(id+"F9.boolean.opBoolean","MERGE",FACE,{"derivedFrom":[makeQuery(id+"F1.opExtrude","SWEPT_FACE",FACE,{"disambiguationData":[OSD([subQ10])]}),makeQuery(id+"F9.opExtrude","SWEPT_FACE",FACE,{"disambiguationData":[OSD([subQ30])]})]});var subQ39=makeQuery(id+"FV3vAcjhJecL5uw_1.1.F13.boolean.opBoolean","SPLIT",FACE,{"disambiguationData":[TD([subQ6])],"derivedFrom":subQ38});var subQ40=makeQuery(id+"FV3vAcjhJecL5uw_1.2.F13.boolean.opBoolean","SPLIT",FACE,{"disambiguationData":[TD([subQ6])],"derivedFrom":subQ39});var subQ41=makeQuery(id+"FPH29GYt6Bfk9Ch_1.1.FAmw6PLWARKAkms_1.1.F13.boolean.opBoolean","SPLIT",FACE,{"disambiguationData":[TD([subQ6])],"derivedFrom":subQ40});Q9=makeQuery(id+"F17.boolean.opBoolean","INTERSECT",EDGE,{"disambiguationData":[OD(0.0)],"derivedFrom":[makeQuery(id+"F15.boolean.opBoolean","MERGE",FACE,{"derivedFrom":[makeQuery(id+"FV3vAcjhJecL5uw_1.1.F13.boolean.opBoolean","SPLIT",FACE,{"disambiguationData":[TD([makeQuery(id+"F13.boolean.opBoolean","COPY",FACE,{"derivedFrom":makeQuery(id+"F13.opExtrude","SWEPT_FACE",FACE,{"disambiguationData":[OSD([subQ3])]})})])],"derivedFrom":subQ38}),makeQuery(id+"FV3vAcjhJecL5uw_1.2.F13.boolean.opBoolean","SPLIT",FACE,{"disambiguationData":[TD([makeQuery(id+"FV3vAcjhJecL5uw_1.1.F13.boolean.opBoolean","COPY",FACE,{"derivedFrom":subQ37})])],"derivedFrom":subQ39}),makeQuery(id+"FPH29GYt6Bfk9Ch_1.1.FAmw6PLWARKAkms_1.1.F13.boolean.opBoolean","SPLIT",FACE,{"disambiguationData":[TD([makeQuery(id+"FAmw6PLWARKAkms_1.1.F13.boolean.opBoolean","COPY",FACE,{"derivedFrom":makeQuery(id+"FAmw6PLWARKAkms_1.1.F13.opExtrude","SWEPT_FACE",FACE,{"disambiguationData":[OSD([subQ3])]})})])],"derivedFrom":subQ40}),makeQuery(id+"FPH29GYt6Bfk9Ch_1.2.FAmw6PLWARKAkms_1.1.F13.boolean.opBoolean","SPLIT",FACE,{"disambiguationData":[TD([makeQuery(id+"FPH29GYt6Bfk9Ch_1.1.FAmw6PLWARKAkms_1.1.F13.boolean.opBoolean","COPY",FACE,{"derivedFrom":subQ36})])],"derivedFrom":subQ41}),makeQuery(id+"FPH29GYt6Bfk9Ch_1.2.FAmw6PLWARKAkms_1.1.F13.boolean.opBoolean","SPLIT",FACE,{"disambiguationData":[TD([subQ6])],"derivedFrom":subQ41}),makeQuery(id+"F15.opExtrude","SWEPT_FACE",FACE,{"disambiguationData":[OSD([sQuery(id+"F14.wireOp",EDGE,"E19")])]})]}),makeQuery(id+"F17.opExtrude","SWEPT_FACE",FACE,{"disambiguationData":[OSD([sQuery(id+"F16.wireOp",EDGE,"E21.top")])]})]});}
            fillet(context, id + "F22", {"entities" : qUnion([Q0, Q1, Q2, Q3, Q4, Q5, Q6, Q7, Q8, Q9]), "radius" : 0.5 * mm, "tangentPropagation" : true, "allowEdgeOverflow" : false});
        }
    });
